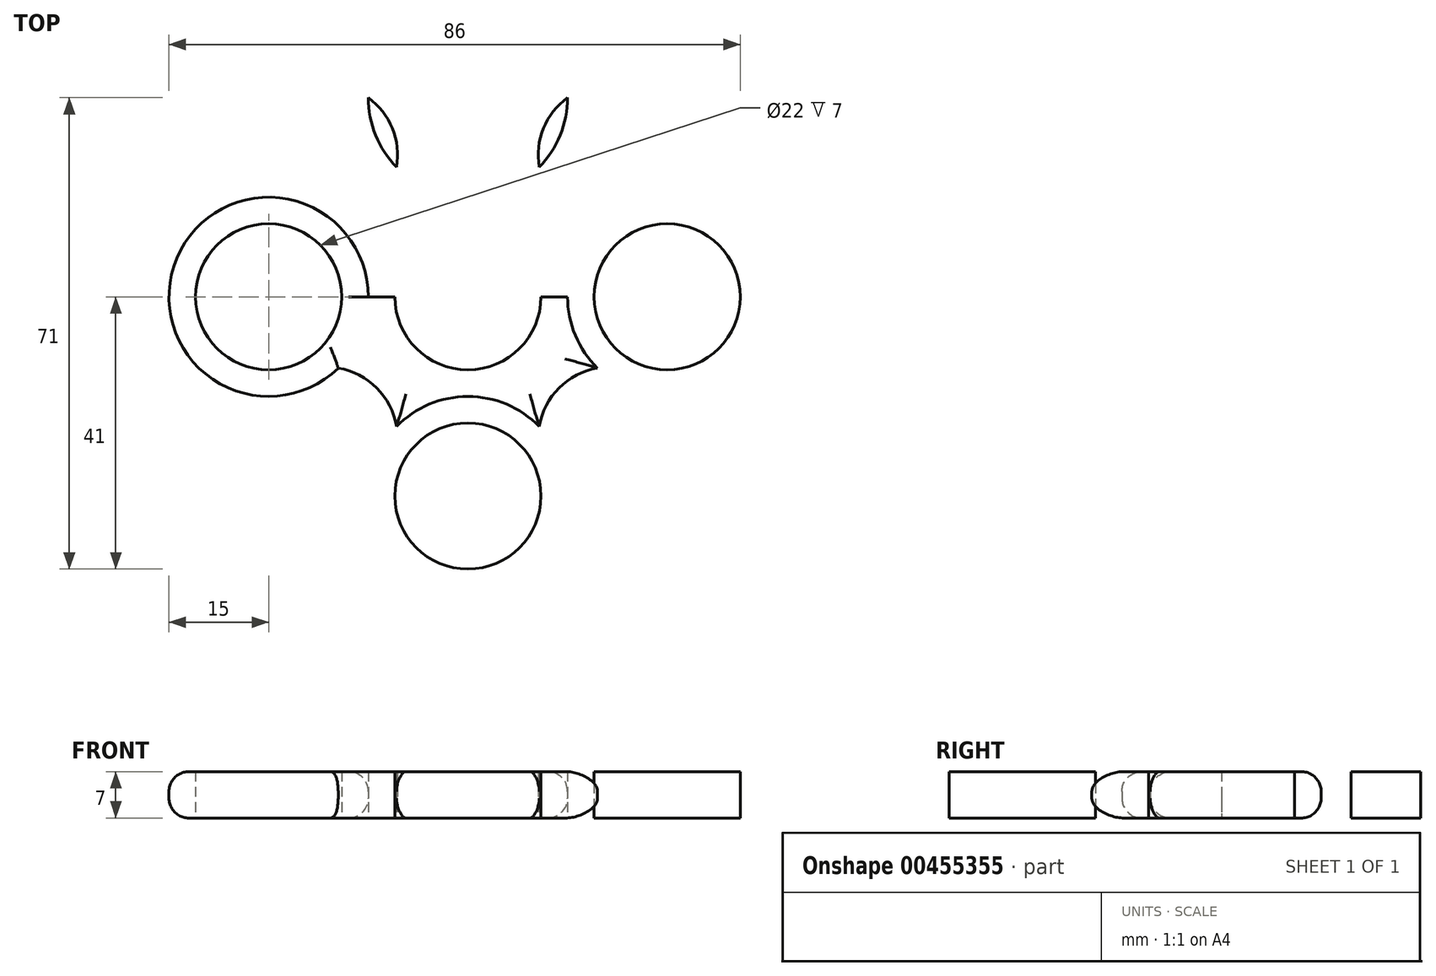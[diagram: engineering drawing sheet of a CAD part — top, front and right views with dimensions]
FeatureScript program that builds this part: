
annotation { "Feature Type Name" : "Feature", "Feature Type Description" : "" }
export const myFeature = defineFeature(function(context is Context, id is Id, definition is map)
    precondition{}
    {
        {
            var Q0;
            Q0=qCreatedBy(makeId("Top.planeOp"),FACE);
            var sketch = newSketch(context, id + "F0", { "sketchPlane" : qUnion([Q0])});
            skLineSegment(sketch, "E0", {"start": v(0, 0) * mm, "end": v(0, 30) * mm});
            skLineSegment(sketch, "E1", {"start": v(0, 30) * mm, "end": v(0, 0) * mm});
            skLineSegment(sketch, "E2", {"start": v(-30, 0) * mm, "end": v(0, 0) * mm});
            skCircle(sketch, "E3", {"center": v(0, 30) * mm, "radius": 11 * mm});
            skCircle(sketch, "E4", {"center": v(-30, 0) * mm, "radius": 11 * mm});
            skLineSegment(sketch, "E5.MirrorCS", {"start": v(30, 0) * mm, "end": v(0, 0) * mm});
            skCircle(sketch, "E6.MirrorC", {"center": v(30, 0) * mm, "radius": 11 * mm});
            skLineSegment(sketch, "E7.MirrorCS", {"start": v(0, -30) * mm, "end": v(0, 0) * mm});
            skCircle(sketch, "E8.MirrorC", {"center": v(0, -30) * mm, "radius": 11 * mm});
            skCircle(sketch, "E9", {"center": v(0, 0) * mm, "radius": 11 * mm});
            skCircle(sketch, "E10", {"center": v(0, 30) * mm, "radius": 15 * mm});
            skCircle(sketch, "E11.MirrorC", {"center": v(0, -30) * mm, "radius": 15 * mm});
            skCircle(sketch, "E12", {"center": v(-30, 0) * mm, "radius": 15 * mm});
            skCircle(sketch, "E13.MirrorC", {"center": v(30, 0) * mm, "radius": 15 * mm});
            skLineSegment(sketch, "E14", {"start": v(0, 30) * mm, "end": v(-15, 30) * mm});
            skLineSegment(sketch, "E15", {"start": v(-30, 0) * mm, "end": v(-30, 15) * mm});
            skArc(sketch, "E16", {"start": v(-30, 15) * mm, "mid": v(-13.73, 13.73) * mm, "end": v(-15, 30) * mm});
            skArc(sketch, "E17.MirrorCS", {"start": v(30, 15) * mm, "mid": v(13.73, 13.73) * mm, "end": v(15, 30) * mm});
            skArc(sketch, "E18.MirrorCS", {"start": v(30, -15) * mm, "mid": v(13.73, -13.73) * mm, "end": v(15, -30) * mm});
            skArc(sketch, "E19.MirrorCS", {"start": v(-30, -15) * mm, "mid": v(-13.73, -13.73) * mm, "end": v(-15, -30) * mm});
            skSolve(sketch);
        }
        {
            var Q0;
            {var subQ1=sQuery(id+"F0.wireOp",EDGE,"E10");var subQ3=sQuery(id+"F0.wireOp",EDGE,"E1");var subQ4=makeQuery(id+"F0.imprint","INTERSECT",VERTEX,{"derivedFrom":[subQ3,subQ1]});Q0=makeQuery(id+"F0.imprint","IMPRINT",FACE,{"disambiguationData":[TD([[makeQuery(id+"F0.imprint","IMPRINT",EDGE,{"disambiguationData":[TD([[subQ4,-1.0]])],"derivedFrom":subQ3}),-1.0]])]});}
            var Q1;
            {var subQ6=sQuery(id+"F0.wireOp",EDGE,"E2");var subQ9=sQuery(id+"F0.wireOp",EDGE,"E12");var subQ10=makeQuery(id+"F0.imprint","INTERSECT",VERTEX,{"derivedFrom":[subQ6,subQ9]});Q1=makeQuery(id+"F0.imprint","IMPRINT",FACE,{"disambiguationData":[TD([[makeQuery(id+"F0.imprint","IMPRINT",EDGE,{"disambiguationData":[TD([[subQ10,-1.0]])],"derivedFrom":subQ6}),-1.0]])]});}
            var Q2;
            {var subQ1=sQuery(id+"F0.wireOp",EDGE,"E10");var subQ3=sQuery(id+"F0.wireOp",EDGE,"E1");var subQ4=makeQuery(id+"F0.imprint","INTERSECT",VERTEX,{"derivedFrom":[subQ3,subQ1]});Q2=makeQuery(id+"F0.imprint","IMPRINT",FACE,{"disambiguationData":[TD([[makeQuery(id+"F0.imprint","IMPRINT",EDGE,{"disambiguationData":[TD([[subQ4,-1.0]])],"derivedFrom":subQ3}),1.0]])]});}
            var Q3;
            {var subQ3=sQuery(id+"F0.wireOp",EDGE,"E1");var subQ8=sQuery(id+"F0.wireOp",EDGE,"E3");var subQ9=makeQuery(id+"F0.imprint","INTERSECT",VERTEX,{"derivedFrom":[subQ3,subQ8]});Q3=makeQuery(id+"F0.imprint","IMPRINT",FACE,{"disambiguationData":[TD([[makeQuery(id+"F0.imprint","IMPRINT",EDGE,{"disambiguationData":[TD([[subQ9,-1.0]])],"derivedFrom":subQ3}),1.0]])]});}
            var Q4;
            {var subQ1=sQuery(id+"F0.wireOp",EDGE,"E5.MirrorCS");var subQ9=sQuery(id+"F0.wireOp",EDGE,"E13.MirrorC");var subQ10=makeQuery(id+"F0.imprint","INTERSECT",VERTEX,{"derivedFrom":[subQ1,subQ9]});Q4=makeQuery(id+"F0.imprint","IMPRINT",FACE,{"disambiguationData":[TD([[makeQuery(id+"F0.imprint","IMPRINT",EDGE,{"disambiguationData":[TD([[subQ10,-1.0]])],"derivedFrom":subQ1}),1.0]])]});}
            var Q5;
            Q5=makeQuery(id+"F0.imprint","IMPRINT",FACE,{"disambiguationData":[TD([[makeQuery(id+"F0.imprint","IMPRINT",EDGE,{"derivedFrom":sQuery(id+"F0.wireOp",EDGE,"E6.MirrorC")}),1.0]])]});
            var Q6;
            {var subQ3=sQuery(id+"F0.wireOp",EDGE,"E2");var subQ5=sQuery(id+"F0.wireOp",EDGE,"E4");var subQ6=makeQuery(id+"F0.imprint","INTERSECT",VERTEX,{"derivedFrom":[subQ3,subQ5]});Q6=makeQuery(id+"F0.imprint","IMPRINT",FACE,{"disambiguationData":[TD([[makeQuery(id+"F0.imprint","IMPRINT",EDGE,{"disambiguationData":[TD([[subQ6,-1.0]])],"derivedFrom":subQ3}),1.0]])]});}
            var Q7;
            {var subQ5=sQuery(id+"F0.wireOp",EDGE,"E4");var subQ8=sQuery(id+"F0.wireOp",EDGE,"E2");var subQ10=makeQuery(id+"F0.imprint","INTERSECT",VERTEX,{"derivedFrom":[subQ8,subQ5]});Q7=makeQuery(id+"F0.imprint","IMPRINT",FACE,{"disambiguationData":[TD([[makeQuery(id+"F0.imprint","IMPRINT",EDGE,{"disambiguationData":[TD([[subQ10,-1.0]])],"derivedFrom":subQ8}),-1.0]])]});}
            var Q8;
            {var subQ0=sQuery(id+"F0.wireOp",EDGE,"E19.MirrorCS");var subQ1=sQuery(id+"F0.wireOp",EDGE,"E12");var subQ2=makeQuery(id+"F0.imprint","INTERSECT",VERTEX,{"disambiguationData":[OD(0.0)],"derivedFrom":[subQ1,subQ0]});Q8=makeQuery(id+"F0.imprint","IMPRINT",FACE,{"disambiguationData":[TD([[makeQuery(id+"F0.imprint","IMPRINT",EDGE,{"disambiguationData":[TD([[subQ2,-1.0]])],"derivedFrom":subQ1}),1.0]])]});}
            var Q9;
            {var subQ0=sQuery(id+"F0.wireOp",EDGE,"E19.MirrorCS");var subQ1=sQuery(id+"F0.wireOp",EDGE,"E11.MirrorC");var subQ2=makeQuery(id+"F0.imprint","INTERSECT",VERTEX,{"disambiguationData":[OD(0.0)],"derivedFrom":[subQ1,subQ0]});Q9=makeQuery(id+"F0.imprint","IMPRINT",FACE,{"disambiguationData":[TD([[makeQuery(id+"F0.imprint","IMPRINT",EDGE,{"disambiguationData":[TD([[subQ2,-1.0]])],"derivedFrom":subQ1}),-1.0]])]});}
            var Q10;
            {var subQ0=sQuery(id+"F0.wireOp",EDGE,"E16");var subQ1=sQuery(id+"F0.wireOp",EDGE,"E10");var subQ3=makeQuery(id+"F0.imprint","INTERSECT",VERTEX,{"derivedFrom":[subQ1,subQ0]});Q10=makeQuery(id+"F0.imprint","IMPRINT",FACE,{"disambiguationData":[TD([[makeQuery(id+"F0.imprint","IMPRINT",EDGE,{"disambiguationData":[TD([[subQ3,1.0]])],"derivedFrom":subQ1}),1.0]])]});}
            var Q11;
            {var subQ3=sQuery(id+"F0.wireOp",EDGE,"E1");var subQ7=sQuery(id+"F0.wireOp",EDGE,"E3");var subQ9=makeQuery(id+"F0.imprint","INTERSECT",VERTEX,{"derivedFrom":[subQ3,subQ7]});Q11=makeQuery(id+"F0.imprint","IMPRINT",FACE,{"disambiguationData":[TD([[makeQuery(id+"F0.imprint","IMPRINT",EDGE,{"disambiguationData":[TD([[subQ9,-1.0]])],"derivedFrom":subQ3}),-1.0]])]});}
            var Q12;
            {var subQ0=sQuery(id+"F0.wireOp",EDGE,"E17.MirrorCS");var subQ1=sQuery(id+"F0.wireOp",EDGE,"E10");var subQ2=makeQuery(id+"F0.imprint","INTERSECT",VERTEX,{"disambiguationData":[OD(0.0)],"derivedFrom":[subQ1,subQ0]});Q12=makeQuery(id+"F0.imprint","IMPRINT",FACE,{"disambiguationData":[TD([[makeQuery(id+"F0.imprint","IMPRINT",EDGE,{"disambiguationData":[TD([[subQ2,1.0]])],"derivedFrom":subQ1}),1.0]])]});}
            var Q13;
            {var subQ0=sQuery(id+"F0.wireOp",EDGE,"E17.MirrorCS");var subQ1=sQuery(id+"F0.wireOp",EDGE,"E13.MirrorC");var subQ2=makeQuery(id+"F0.imprint","INTERSECT",VERTEX,{"disambiguationData":[OD(0.0)],"derivedFrom":[subQ1,subQ0]});Q13=makeQuery(id+"F0.imprint","IMPRINT",FACE,{"disambiguationData":[TD([[makeQuery(id+"F0.imprint","IMPRINT",EDGE,{"disambiguationData":[TD([[subQ2,1.0]])],"derivedFrom":subQ1}),-1.0]])]});}
            var Q14;
            {var subQ0=sQuery(id+"F0.wireOp",EDGE,"E18.MirrorCS");var subQ1=sQuery(id+"F0.wireOp",EDGE,"E11.MirrorC");var subQ2=makeQuery(id+"F0.imprint","INTERSECT",VERTEX,{"disambiguationData":[OD(0.0)],"derivedFrom":[subQ1,subQ0]});Q14=makeQuery(id+"F0.imprint","IMPRINT",FACE,{"disambiguationData":[TD([[makeQuery(id+"F0.imprint","IMPRINT",EDGE,{"disambiguationData":[TD([[subQ2,1.0]])],"derivedFrom":subQ1}),-1.0]])]});}
            var Q15;
            Q15=makeQuery(id+"F0.imprint","IMPRINT",FACE,{"disambiguationData":[TD([[makeQuery(id+"F0.imprint","IMPRINT",EDGE,{"derivedFrom":sQuery(id+"F0.wireOp",EDGE,"E8.MirrorC")}),1.0]])]});
            var Q16;
            {var subQ0=sQuery(id+"F0.wireOp",EDGE,"E18.MirrorCS");var subQ1=sQuery(id+"F0.wireOp",EDGE,"E13.MirrorC");var subQ2=makeQuery(id+"F0.imprint","INTERSECT",VERTEX,{"disambiguationData":[OD(0.0)],"derivedFrom":[subQ1,subQ0]});Q16=makeQuery(id+"F0.imprint","IMPRINT",FACE,{"disambiguationData":[TD([[makeQuery(id+"F0.imprint","IMPRINT",EDGE,{"disambiguationData":[TD([[subQ2,-1.0]])],"derivedFrom":subQ1}),-1.0]])]});}
            var Q17;
            {var subQ0=sQuery(id+"F0.wireOp",EDGE,"E16");var subQ1=sQuery(id+"F0.wireOp",EDGE,"E12");var subQ3=makeQuery(id+"F0.imprint","INTERSECT",VERTEX,{"derivedFrom":[subQ1,subQ0]});Q17=makeQuery(id+"F0.imprint","IMPRINT",FACE,{"disambiguationData":[TD([[makeQuery(id+"F0.imprint","IMPRINT",EDGE,{"disambiguationData":[TD([[subQ3,-1.0]])],"derivedFrom":subQ1}),1.0]])]});}
            extrude(context, id + "F1", {"entities" : qUnion([Q0, Q1, Q2, Q3, Q4, Q5, Q6, Q7, Q8, Q9, Q10, Q11, Q12, Q13, Q14, Q15, Q16, Q17]), "depth" : 7 * mm});
        }
        {
            var Q0;
            Q0=makeQuery(id+"F1.opExtrude","CAP_EDGE",EDGE,{"disambiguationData":[OSD([sQuery(id+"F0.wireOp",EDGE,"E18.MirrorCS")])],"isStart":true});
            var Q1;
            Q1=makeQuery(id+"F1.opExtrude","CAP_EDGE",EDGE,{"disambiguationData":[OSD([sQuery(id+"F0.wireOp",EDGE,"E11.MirrorC")])],"isStart":true});
            var Q2;
            Q2=makeQuery(id+"F1.opExtrude","CAP_EDGE",EDGE,{"disambiguationData":[OSD([sQuery(id+"F0.wireOp",EDGE,"E13.MirrorC")])],"isStart":true});
            var Q3;
            Q3=makeQuery(id+"F1.opExtrude","CAP_EDGE",EDGE,{"disambiguationData":[OSD([sQuery(id+"F0.wireOp",EDGE,"E17.MirrorCS")])],"isStart":true});
            var Q4;
            Q4=makeQuery(id+"F1.opExtrude","CAP_EDGE",EDGE,{"disambiguationData":[OSD([sQuery(id+"F0.wireOp",EDGE,"E10")])],"isStart":true});
            var Q5;
            Q5=makeQuery(id+"F1.opExtrude","CAP_EDGE",EDGE,{"disambiguationData":[OSD([sQuery(id+"F0.wireOp",EDGE,"E16")])],"isStart":true});
            var Q6;
            Q6=makeQuery(id+"F1.opExtrude","CAP_EDGE",EDGE,{"disambiguationData":[OSD([sQuery(id+"F0.wireOp",EDGE,"E12")])],"isStart":true});
            var Q7;
            Q7=makeQuery(id+"F1.opExtrude","CAP_EDGE",EDGE,{"disambiguationData":[OSD([sQuery(id+"F0.wireOp",EDGE,"E19.MirrorCS")])],"isStart":true});
            fillet(context, id + "F2", {"entities" : qUnion([Q0, Q1, Q2, Q3, Q4, Q5, Q6, Q7]), "radius" : 3 * mm, "tangentPropagation" : true, "allowEdgeOverflow" : false});
        }
        {
            var Q0;
            Q0=makeQuery(id+"F1.opExtrude","CAP_EDGE",EDGE,{"disambiguationData":[OSD([sQuery(id+"F0.wireOp",EDGE,"E11.MirrorC")])],"isStart":false});
            var Q1;
            Q1=makeQuery(id+"F1.opExtrude","CAP_EDGE",EDGE,{"disambiguationData":[OSD([sQuery(id+"F0.wireOp",EDGE,"E18.MirrorCS")])],"isStart":false});
            var Q2;
            Q2=makeQuery(id+"F1.opExtrude","CAP_EDGE",EDGE,{"disambiguationData":[OSD([sQuery(id+"F0.wireOp",EDGE,"E13.MirrorC")])],"isStart":false});
            var Q3;
            Q3=makeQuery(id+"F1.opExtrude","CAP_EDGE",EDGE,{"disambiguationData":[OSD([sQuery(id+"F0.wireOp",EDGE,"E17.MirrorCS")])],"isStart":false});
            var Q4;
            Q4=makeQuery(id+"F1.opExtrude","CAP_EDGE",EDGE,{"disambiguationData":[OSD([sQuery(id+"F0.wireOp",EDGE,"E10")])],"isStart":false});
            var Q5;
            Q5=makeQuery(id+"F1.opExtrude","CAP_EDGE",EDGE,{"disambiguationData":[OSD([sQuery(id+"F0.wireOp",EDGE,"E16")])],"isStart":false});
            var Q6;
            Q6=makeQuery(id+"F1.opExtrude","CAP_EDGE",EDGE,{"disambiguationData":[OSD([sQuery(id+"F0.wireOp",EDGE,"E12")])],"isStart":false});
            var Q7;
            Q7=makeQuery(id+"F1.opExtrude","CAP_EDGE",EDGE,{"disambiguationData":[OSD([sQuery(id+"F0.wireOp",EDGE,"E19.MirrorCS")])],"isStart":false});
            fillet(context, id + "F3", {"entities" : qUnion([Q0, Q1, Q2, Q3, Q4, Q5, Q6, Q7]), "radius" : 3 * mm, "tangentPropagation" : true, "allowEdgeOverflow" : false});
        }
    });
